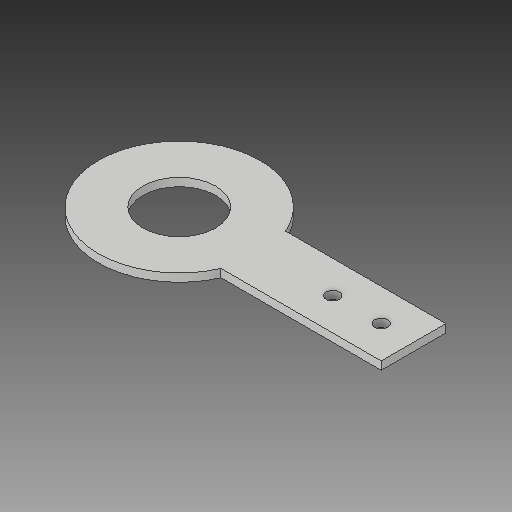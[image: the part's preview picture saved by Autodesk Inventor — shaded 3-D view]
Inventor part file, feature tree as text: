
AUTODESK INVENTOR PART (.ipt)
format: ipt  version: 2018 (Build 220112000, 112)  size: 96,768 bytes
history: native  units: in
note: dims shown in document units (in); Inventor stores cm internally (conversion verified against a paired STEP export)
features: other x3, sketch x1
ambient origin geometry x8: Origin, YZ Plane, XZ Plane, XY Plane, X Axis, Y Axis, Z Axis, Center Point
bodies: Solid1 (feature_tree)
feature tree (4):
  other  "wheel tip.ipt"
  other  "Solid1::wheel tip.ipt"
  other  "TaggingFeature1"
  sketch  "Sketch1"  dims[d0=0.3937in]
